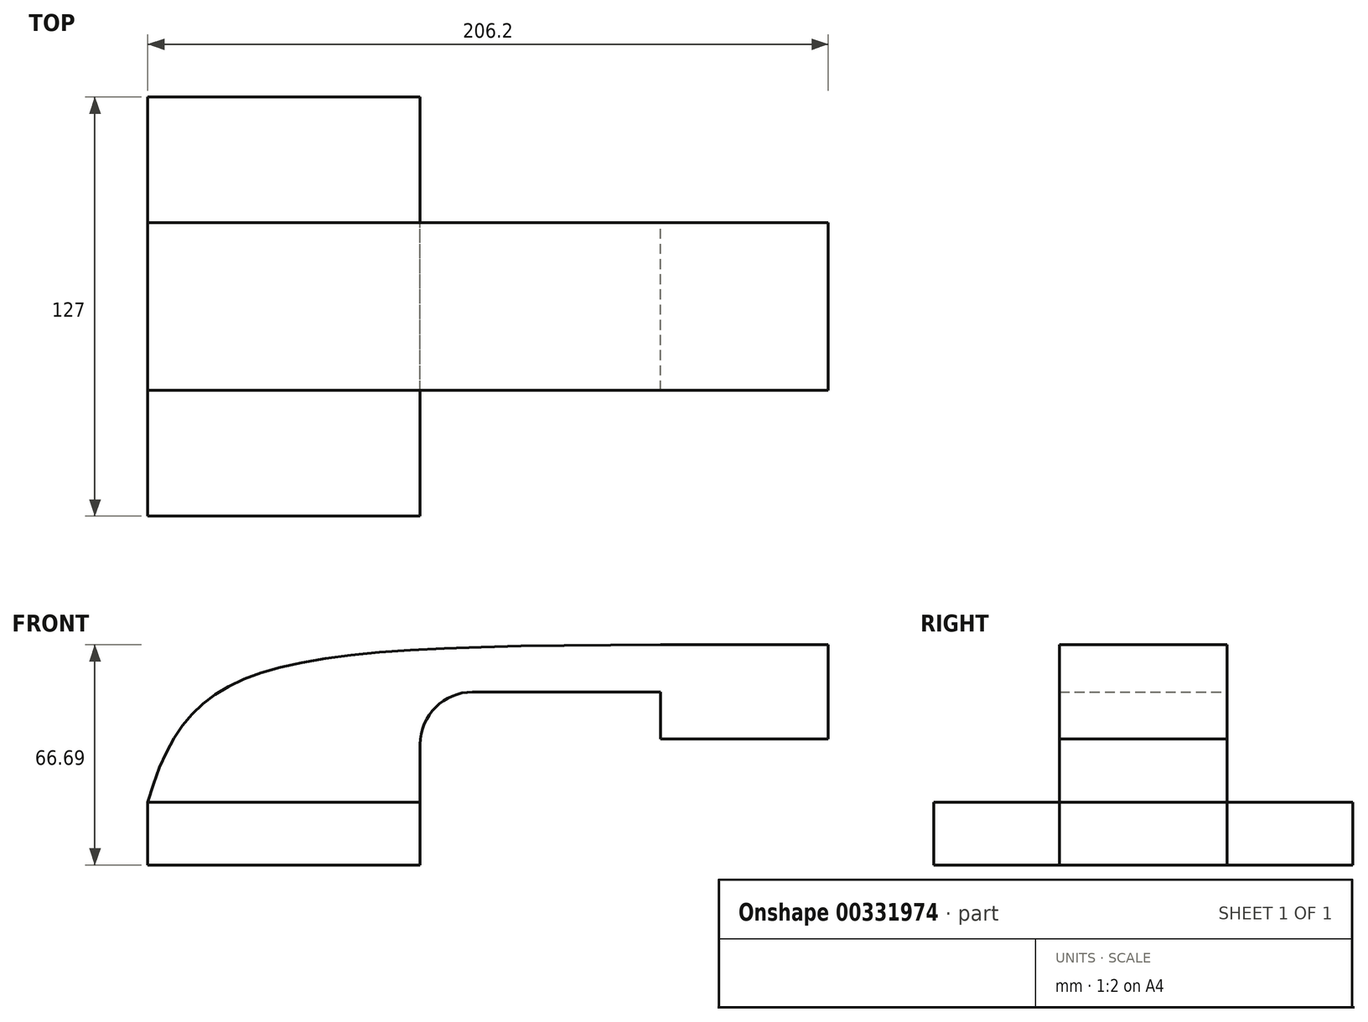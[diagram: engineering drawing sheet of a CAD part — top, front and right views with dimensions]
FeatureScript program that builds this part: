
annotation { "Feature Type Name" : "Feature", "Feature Type Description" : "" }
export const myFeature = defineFeature(function(context is Context, id is Id, definition is map)
    precondition{}
    {
        {
            var Q0;
            Q0=qCreatedBy(makeId("Front.planeOp"),FACE);
            var sketch = newSketch(context, id + "F0", { "sketchPlane" : qUnion([Q0])});
            skLineSegment(sketch, "E0.bottom", {"start": v(-41.28, -9.53) * mm, "end": v(41.28, -9.53) * mm});
            skLineSegment(sketch, "E0.top", {"start": v(-41.28, 9.53) * mm, "end": v(41.28, 9.53) * mm});
            skLineSegment(sketch, "E0.left", {"start": v(-41.28, -9.53) * mm, "end": v(-41.28, 9.53) * mm});
            skLineSegment(sketch, "E0.right", {"start": v(41.28, -9.53) * mm, "end": v(41.28, 9.53) * mm});
            skPoint(sketch, "E0.middle", {"position": v(0, 0) * mm});
            skLineSegment(sketch, "E1.bottom", {"start": v(114.12, 28.59) * mm, "end": v(164.92, 28.59) * mm});
            skLineSegment(sketch, "E1.top", {"start": v(114.12, 57.16) * mm, "end": v(164.92, 57.16) * mm});
            skLineSegment(sketch, "E1.left", {"start": v(114.12, 28.59) * mm, "end": v(114.12, 57.16) * mm});
            skLineSegment(sketch, "E1.right", {"start": v(164.92, 28.59) * mm, "end": v(164.92, 57.16) * mm});
            skPoint(sketch, "E1.middle", {"position": v(139.52, 42.88) * mm});
            skLineSegment(sketch, "E2", {"start": v(41.28, 9.53) * mm, "end": v(41.28, 27) * mm});
            skArc(sketch, "E3", {"start": v(41.28, 27) * mm, "mid": v(45.92, 38.23) * mm, "end": v(57.15, 42.88) * mm});
            skPoint(sketch, "E4", {"position": v(114.12, 42.88) * mm});
            skLineSegment(sketch, "E5", {"start": v(57.15, 42.88) * mm, "end": v(139.52, 42.88) * mm});
            skLineSegment(sketch, "E6.0", {"start": v(57.15, 53.92) * mm, "end": v(139.63, 53.92) * mm});
            skArc(sketch, "E6.1", {"start": v(30.23, 27) * mm, "mid": v(38.11, 46.04) * mm, "end": v(57.15, 53.92) * mm});
            skLineSegment(sketch, "E6.2", {"start": v(30.23, 9.53) * mm, "end": v(30.23, 27) * mm});
            skFitSpline(sketch, "E7", {"points": [v(-41.28, 9.53) * mm, v(114.12, 57.16) * mm], "startDerivative": vector(37.46, 130.77) * mm, "endDerivative": vector(361.36, 0.91) * mm});
            skSolve(sketch);
        }
        {
            var Q0;
            Q0=makeQuery(id+"F0.imprint","IMPRINT",FACE,{"disambiguationData":[TD([[makeQuery(id+"F0.imprint","IMPRINT",EDGE,{"derivedFrom":sQuery(id+"F0.wireOp",EDGE,"E0.bottom")}),1.0]])]});
            extrude(context, id + "F1", {"entities" : qUnion([Q0]), "endBound" : BoundingType.SYMMETRIC, "depth" : 127 * mm});
        }
        {
            var Q0;
            Q0 = qSketchRegion(id + "F0", true);
            extrude(context, id + "F2", {"entities" : qUnion([Q0]), "endBound" : BoundingType.SYMMETRIC, "depth" : 50.8 * mm});
        }
    });
